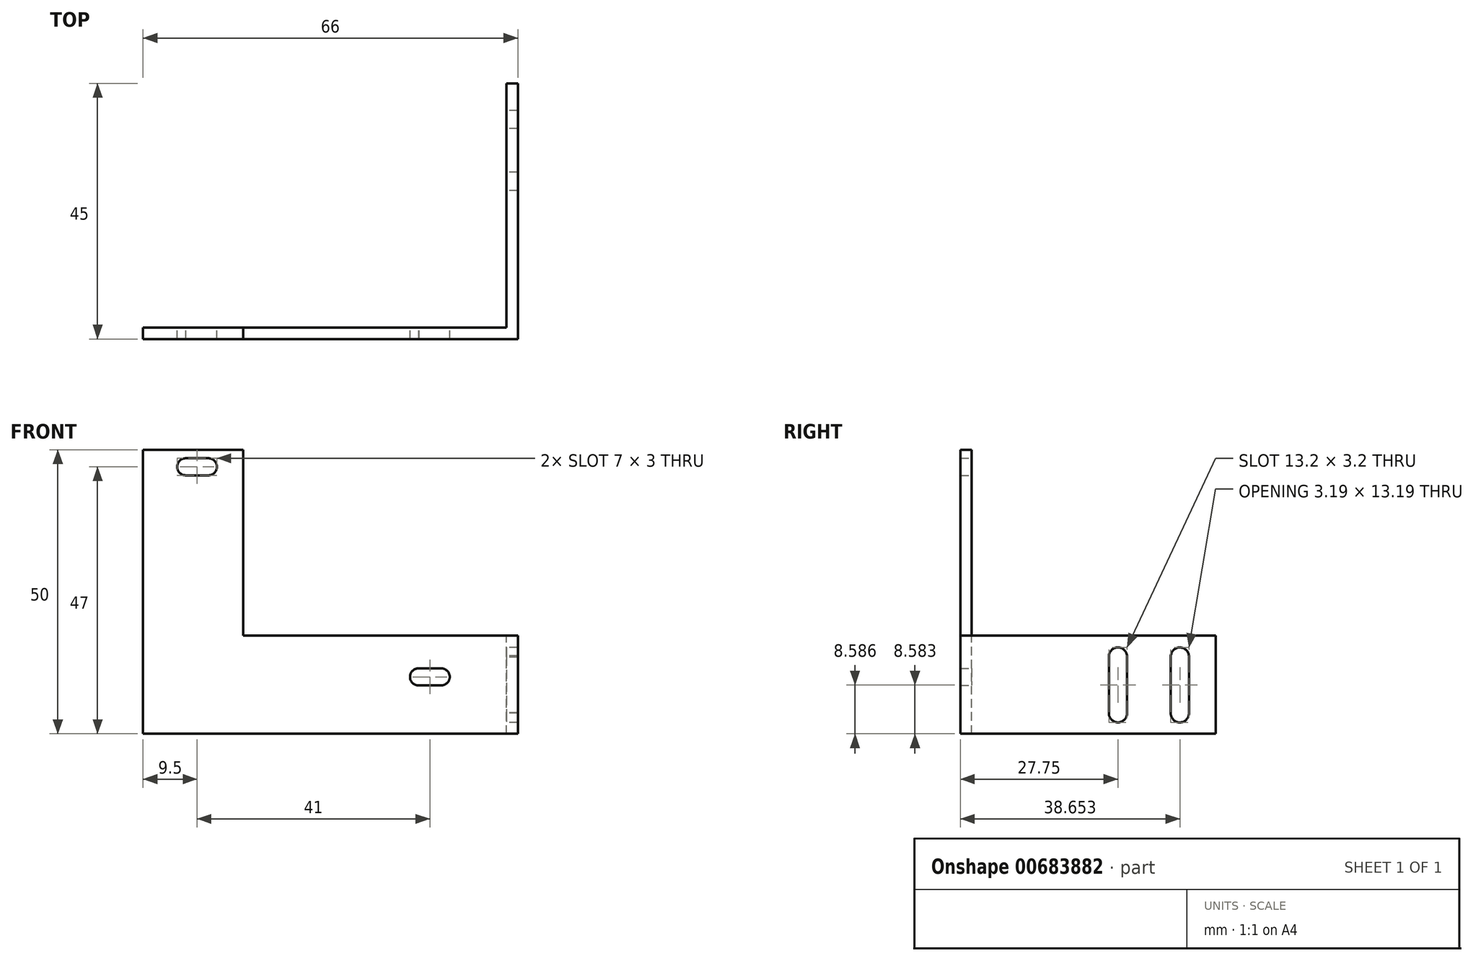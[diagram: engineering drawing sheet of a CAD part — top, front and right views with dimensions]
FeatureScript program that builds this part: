
annotation { "Feature Type Name" : "Feature", "Feature Type Description" : "" }
export const myFeature = defineFeature(function(context is Context, id is Id, definition is map)
    precondition{}
    {
        {
            var Q0;
            Q0=qCreatedBy(makeId("Front.planeOp"),FACE);
            var sketch = newSketch(context, id + "F0", { "sketchPlane" : qUnion([Q0])});
            skLineSegment(sketch, "E0.bottom", {"start": v(32.5, -25) * mm, "end": v(-32.5, -25) * mm});
            skLineSegment(sketch, "E0.top", {"start": v(32.5, 25) * mm, "end": v(-32.5, 25) * mm});
            skLineSegment(sketch, "E0.left", {"start": v(32.5, -25) * mm, "end": v(32.5, 25) * mm});
            skLineSegment(sketch, "E0.right", {"start": v(-32.5, -25) * mm, "end": v(-32.5, 25) * mm});
            skPoint(sketch, "E0.middle", {"position": v(0, 0) * mm});
            skCircle(sketch, "E1", {"center": v(-25, 22) * mm, "radius": 1.5 * mm});
            skCircle(sketch, "E2", {"center": v(-21, 22) * mm, "radius": 1.5 * mm});
            skLineSegment(sketch, "E3", {"start": v(-24.98, 23.5) * mm, "end": v(-21, 23.5) * mm});
            skLineSegment(sketch, "E4", {"start": v(-25.06, 20.5) * mm, "end": v(-21, 20.5) * mm});
            skCircle(sketch, "E5", {"center": v(16, -15) * mm, "radius": 1.5 * mm});
            skCircle(sketch, "E6", {"center": v(20, -15) * mm, "radius": 1.5 * mm});
            skLineSegment(sketch, "E7", {"start": v(15.98, -13.5) * mm, "end": v(20, -13.5) * mm});
            skLineSegment(sketch, "E8", {"start": v(15.9, -16.5) * mm, "end": v(20, -16.5) * mm});
            skLineSegment(sketch, "E9", {"start": v(-14.85, 25) * mm, "end": v(-14.85, -7.7) * mm});
            skLineSegment(sketch, "E10", {"start": v(-14.85, -7.7) * mm, "end": v(32.5, -7.7) * mm});
            skSolve(sketch);
        }
        {
            var Q0;
            Q0=makeQuery(id+"F0.imprint","IMPRINT",FACE,{"disambiguationData":[TD([[makeQuery(id+"F0.imprint","IMPRINT",EDGE,{"derivedFrom":sQuery(id+"F0.wireOp",EDGE,"E0.bottom")}),-1.0]])]});
            extrude(context, id + "F1", {"entities" : qUnion([Q0]), "endBound" : BoundingType.SYMMETRIC, "depth" : 2 * mm, "offsetDistance" : 25 * mm});
        }
        {
            var Q0;
            Q0=makeQuery(id+"F1.opExtrude","SWEPT_FACE",FACE,{"disambiguationData":[OSD([sQuery(id+"F0.wireOp",EDGE,"E0.left")])]});
            var sketch = newSketch(context, id + "F2", { "sketchPlane" : qUnion([Q0])});
            skLineSegment(sketch, "E11.bottom", {"start": v(-1, -25) * mm, "end": v(44, -25) * mm});
            skLineSegment(sketch, "E11.top", {"start": v(-1, -7.7) * mm, "end": v(44, -7.7) * mm});
            skLineSegment(sketch, "E11.left", {"start": v(-1, -25) * mm, "end": v(-1, -7.7) * mm});
            skLineSegment(sketch, "E11.right", {"start": v(44, -25) * mm, "end": v(44, -7.7) * mm});
            skCircle(sketch, "E12", {"center": v(37.65, -21.41) * mm, "radius": 1.6 * mm});
            skCircle(sketch, "E13", {"center": v(26.75, -21.41) * mm, "radius": 1.6 * mm});
            skCircle(sketch, "E14", {"center": v(26.75, -11.41) * mm, "radius": 1.6 * mm});
            skCircle(sketch, "E15", {"center": v(37.65, -11.41) * mm, "radius": 1.6 * mm});
            skLineSegment(sketch, "E16.bottom", {"start": v(25.15, -11.38) * mm, "end": v(28.35, -11.38) * mm});
            skLineSegment(sketch, "E16.top", {"start": v(25.15, -21.37) * mm, "end": v(28.35, -21.37) * mm});
            skLineSegment(sketch, "E16.left", {"start": v(25.15, -11.38) * mm, "end": v(25.15, -21.37) * mm});
            skLineSegment(sketch, "E16.right", {"start": v(28.35, -11.38) * mm, "end": v(28.35, -21.37) * mm});
            skLineSegment(sketch, "E17.bottom", {"start": v(36.06, -11.29) * mm, "end": v(39.25, -11.29) * mm});
            skLineSegment(sketch, "E17.top", {"start": v(36.06, -21.37) * mm, "end": v(39.25, -21.37) * mm});
            skLineSegment(sketch, "E17.left", {"start": v(36.06, -11.29) * mm, "end": v(36.06, -21.37) * mm});
            skLineSegment(sketch, "E17.right", {"start": v(39.25, -11.29) * mm, "end": v(39.25, -21.37) * mm});
            skSolve(sketch);
        }
        {
            var Q0;
            Q0 = qSketchRegion(id + "F2", true);
            extrude(context, id + "F3", {"entities" : qUnion([Q0]), "operationType" : NewBodyOperationType.ADD, "endBound" : BoundingType.SYMMETRIC, "depth" : 2 * mm, "offsetDistance" : 25 * mm});
        }
    });
